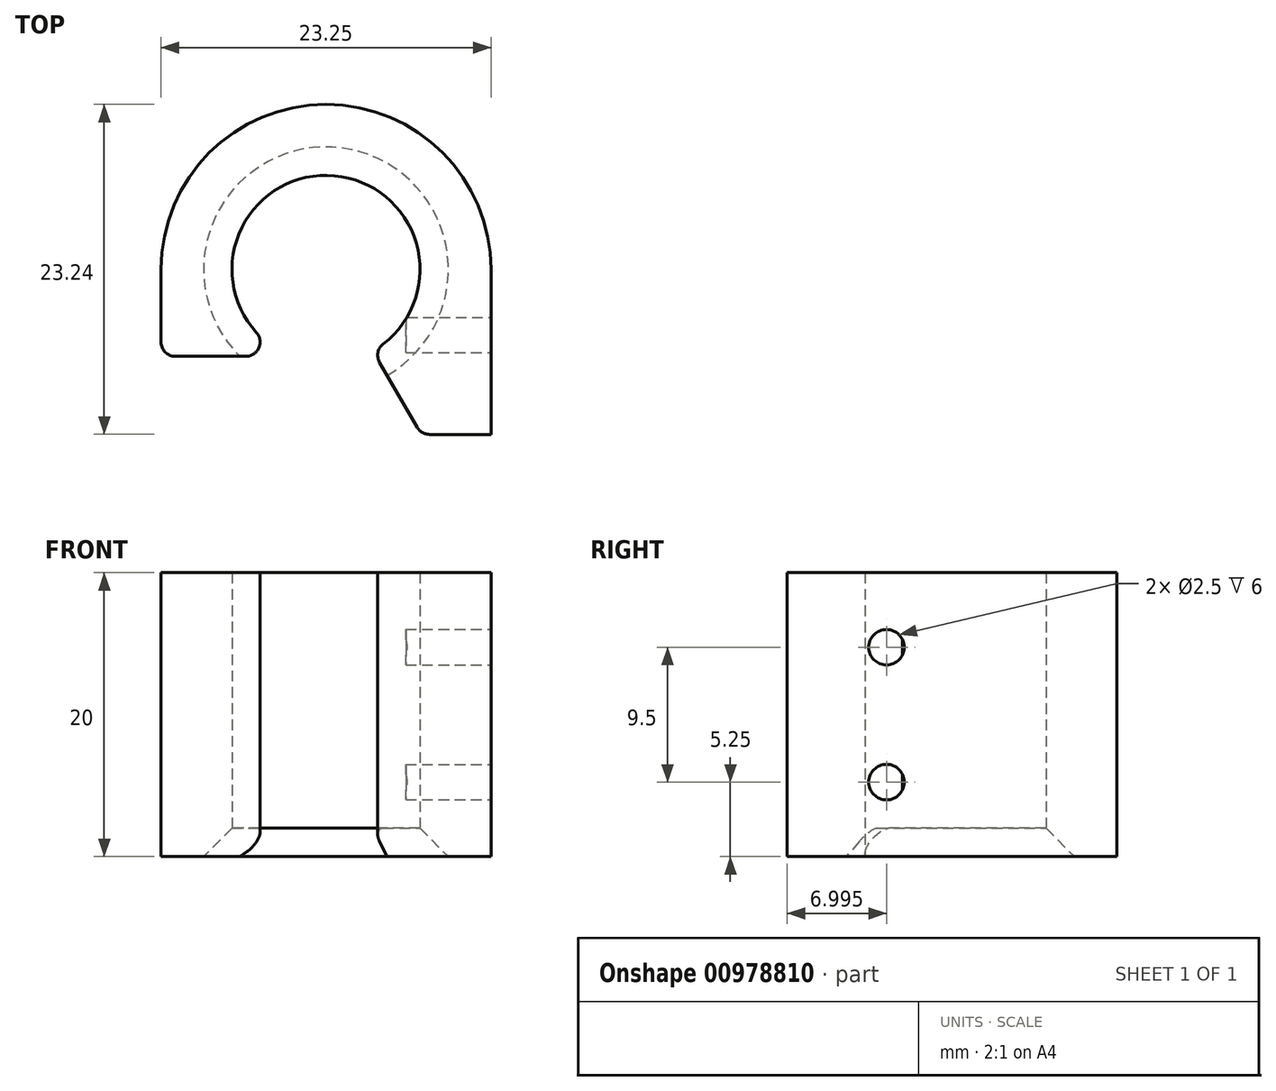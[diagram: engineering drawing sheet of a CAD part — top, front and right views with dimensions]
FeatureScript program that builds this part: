
annotation { "Feature Type Name" : "Feature", "Feature Type Description" : "" }
export const myFeature = defineFeature(function(context is Context, id is Id, definition is map)
    precondition{}
    {
        {
            var Q0;
            Q0=qCreatedBy(makeId("Top.planeOp"),FACE);
            var sketch = newSketch(context, id + "F0", { "sketchPlane" : qUnion([Q0])});
            skArc(sketch, "E0", {"start": v(11.62, 0) * mm, "mid": v(0, 11.62) * mm, "end": v(-11.62, 0) * mm});
            skLineSegment(sketch, "E1.top", {"start": v(11.62, -11.62) * mm, "end": v(7.29, -11.62) * mm});
            skLineSegment(sketch, "E1.left", {"start": v(11.62, 0) * mm, "end": v(11.63, -11.63) * mm});
            skLineSegment(sketch, "E2", {"start": v(0, -11.62) * mm, "end": v(6.71, -11.62) * mm, "construction": true});
            skLineSegment(sketch, "E3", {"start": v(0, 0) * mm, "end": v(0, -11.62) * mm, "construction": true});
            skLineSegment(sketch, "E4", {"start": v(3.78, -6.55) * mm, "end": v(6.42, -11.13) * mm});
            skLineSegment(sketch, "E5.MirrorCS", {"start": v(-3.31, -5.74) * mm, "end": v(-3.54, -6.13) * mm, "construction": true});
            skLineSegment(sketch, "E6", {"start": v(-6.71, -11.63) * mm, "end": v(-11.62, -11.63) * mm, "construction": true});
            skLineSegment(sketch, "E7", {"start": v(-11.62, -11.63) * mm, "end": v(-11.62, -6.13) * mm, "construction": true});
            skArc(sketch, "E8", {"start": v(-3.31, -5.74) * mm, "mid": v(0, -6.63) * mm, "end": v(3.31, -5.74) * mm, "construction": true});
            skArc(sketch, "E9", {"start": v(4.04, -5.25) * mm, "mid": v(0.6, 6.6) * mm, "end": v(-4.9, -4.45) * mm});
            skLineSegment(sketch, "E10", {"start": v(0, -6.12) * mm, "end": v(-3.54, -6.12) * mm, "construction": true});
            skLineSegment(sketch, "E11", {"start": v(-11.62, -5.13) * mm, "end": v(-11.62, 0) * mm});
            skLineSegment(sketch, "E12", {"start": v(-3.54, -6.13) * mm, "end": v(-6.71, -11.63) * mm, "construction": true});
            skLineSegment(sketch, "E13", {"start": v(-3.54, -6.12) * mm, "end": v(-5.65, -6.12) * mm, "construction": true});
            skLineSegment(sketch, "E14", {"start": v(-4.9, -4.45) * mm, "end": v(-4.9, -4.45) * mm});
            skArc(sketch, "E15", {"start": v(-4.9, -4.45) * mm, "mid": v(-4.16, -5.16) * mm, "end": v(-3.31, -5.74) * mm, "construction": true});
            skArc(sketch, "E16", {"start": v(-5.65, -6.13) * mm, "mid": v(-4.73, -5.53) * mm, "end": v(-4.9, -4.45) * mm});
            skArc(sketch, "E17", {"start": v(-4.9, -4.45) * mm, "mid": v(-6.56, -4.72) * mm, "end": v(-5.65, -6.13) * mm, "construction": true});
            skLineSegment(sketch, "E18", {"start": v(-5.65, -6.12) * mm, "end": v(-10.62, -6.13) * mm});
            skPoint(sketch, "E19.visualSharp", {"position": v(3.31, -5.74) * mm});
            skArc(sketch, "E19.filletArc", {"start": v(4.04, -5.25) * mm, "mid": v(3.66, -5.85) * mm, "end": v(3.78, -6.55) * mm});
            skPoint(sketch, "E20.visualSharp", {"position": v(6.71, -11.63) * mm});
            skArc(sketch, "E20.filletArc", {"start": v(6.42, -11.13) * mm, "mid": v(6.79, -11.5) * mm, "end": v(7.29, -11.62) * mm});
            skPoint(sketch, "E21.visualSharp", {"position": v(-11.62, -6.13) * mm});
            skArc(sketch, "E21.filletArc", {"start": v(-11.63, -5.13) * mm, "mid": v(-11.33, -5.83) * mm, "end": v(-10.62, -6.13) * mm});
            skSolve(sketch);
        }
        {
            var Q0;
            Q0=makeQuery(id+"F0.imprint","IMPRINT",FACE,{"disambiguationData":[TD([[makeQuery(id+"F0.imprint","IMPRINT",EDGE,{"derivedFrom":sQuery(id+"F0.wireOp",EDGE,"To4PjYR5-xo9o-pY7b-4j9g-kayWnZ9pAqeV")}),-1.0]])]});
            var Q1;
            Q1=makeQuery(id+"F0.imprint","IMPRINT",FACE,{"disambiguationData":[TD([[makeQuery(id+"F0.imprint","IMPRINT",EDGE,{"derivedFrom":sQuery(id+"F0.wireOp",EDGE,"E0")}),1.0]])]});
            extrude(context, id + "F1", {"entities" : qUnion([Q0, Q1]), "depth" : 20 * mm, "offsetDistance" : 25 * mm});
        }
        {
            var Q0;
            Q0=makeQuery(id+"F1.opExtrude","SWEPT_FACE",FACE,{"disambiguationData":[OSD([sQuery(id+"F0.wireOp",EDGE,"E1.left")])]});
            var sketch = newSketch(context, id + "F2", { "sketchPlane" : qUnion([Q0])});
            skCircle(sketch, "E22", {"center": v(-4.63, 14.75) * mm, "radius": 1.25 * mm});
            skCircle(sketch, "E23", {"center": v(-4.63, 5.25) * mm, "radius": 1.25 * mm});
            skLineSegment(sketch, "E24", {"start": v(-4.63, 5.25) * mm, "end": v(-4.63, 14.75) * mm, "construction": true});
            skLineSegment(sketch, "E25", {"start": v(-4.63, 10) * mm, "end": v(-11.63, 10) * mm, "construction": true});
            skSolve(sketch);
        }
        {
            var Q0;
            Q0=makeQuery(id+"F2.imprint","IMPRINT",FACE,{"disambiguationData":[TD([[makeQuery(id+"F2.imprint","IMPRINT",EDGE,{"derivedFrom":sQuery(id+"F2.wireOp",EDGE,"E22")}),1.0]])]});
            var Q1;
            Q1=makeQuery(id+"F2.imprint","IMPRINT",FACE,{"disambiguationData":[TD([[makeQuery(id+"F2.imprint","IMPRINT",EDGE,{"derivedFrom":sQuery(id+"F2.wireOp",EDGE,"E23")}),1.0]])]});
            extrude(context, id + "F3", {"entities" : qUnion([Q0, Q1]), "operationType" : NewBodyOperationType.REMOVE, "oppositeDirection" : true, "depth" : 6 * mm, "offsetDistance" : 25 * mm});
        }
        {
            var Q0;
            Q0=makeQuery(id+"F1.opExtrude","CAP_EDGE",EDGE,{"disambiguationData":[OSD([sQuery(id+"F0.wireOp",EDGE,"E9")])],"isStart":true});
            chamfer(context, id + "F4", {"entities" : qUnion([Q0]), "width" : 2 * mm});
        }
    });
